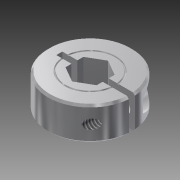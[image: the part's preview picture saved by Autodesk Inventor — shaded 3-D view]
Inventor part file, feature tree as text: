
AUTODESK INVENTOR PART (.ipt)
format: ipt  version: 2016 SP1 (Build 200210100, 210)  size: 417,280 bytes
history: native  units: mm
features: sketch x6, extrude x4, hole x2, other x2, surface_op x1, thread x1, projected_geometry x1
ambient origin geometry x8: Origin, YZ Plane, XZ Plane, XY Plane, X Axis, Y Axis, Z Axis, Center Point
bodies: Solid1 (feature_tree)
feature tree (17):
  surface_op  "Stitch Surface1"
  thread  "Thread1"  [1 undecoded]
  hole  "Hole1"  [1 undecoded]
  extrude  "Extrusion1"  Depth=10.0mm TaperAngle=0.0deg
  hole  "Hole2"  [1 undecoded]
  extrude  "Extrusion2"  [1 undecoded]
  extrude  "Extrusion3"  [1 undecoded]
  extrude  "Extrusion4"  [1 undecoded]
  sketch  "Sketch1"  dims[d2=3.797mm d3=6.0mm d4=12.7mm d5=2.362mm d6=14.3117mm d7=8.0mm d8=20.594885mm d9=9.25mm d10=0.0mm]
  sketch  "Sketch2"  dims[d11=2.642mm d12=10.0mm d13=12.7mm d14=2.362mm d15=14.3117mm d16=8.0mm d17=20.594885mm d18=8.5mm d19=0.0mm]
  sketch  "Sketch3"  dims[d20=9.525mm d21=10.0mm d22=0.0mm]
  projected_geometry  "Projected Loop1"
  sketch  "Sketch4"  dims[d23=10.0mm d24=0.0mm]
  sketch  "Sketch5"
  sketch  "Sketch6"
  other  "Composite1"
  other  "Srf1"
note: 6 required parameter values undecoded (feature->parameter linkage not recoverable at this tier; creation-order binding heuristic only, values carry confidence <= 0.55)
